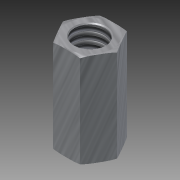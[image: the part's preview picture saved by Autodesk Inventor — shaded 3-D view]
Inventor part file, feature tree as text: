
AUTODESK INVENTOR PART (.ipt)
format: ipt  version: 2011 (Build 150239000, 239)  size: 125,440 bytes
history: native  units: in
note: dims shown in document units (in); Inventor stores cm internally (conversion verified against a paired STEP export)
features: other x1, imported_body x1, thread x1
ambient origin geometry x8: Origin, YZ Plane, XZ Plane, XY Plane, X Axis, Y Axis, Z Axis, Center Point
feature tree (3):
  parser-record x1  (decoder bookkeeping rows leaked as tree rows — omitted from the tree; the rows remain in map.json)
  imported_body  "Base1"
  thread  "Thread1"  [1 undecoded]
note: 1 required parameter value undecoded (feature->parameter linkage not recoverable at this tier; creation-order binding heuristic only, values carry confidence <= 0.55)
